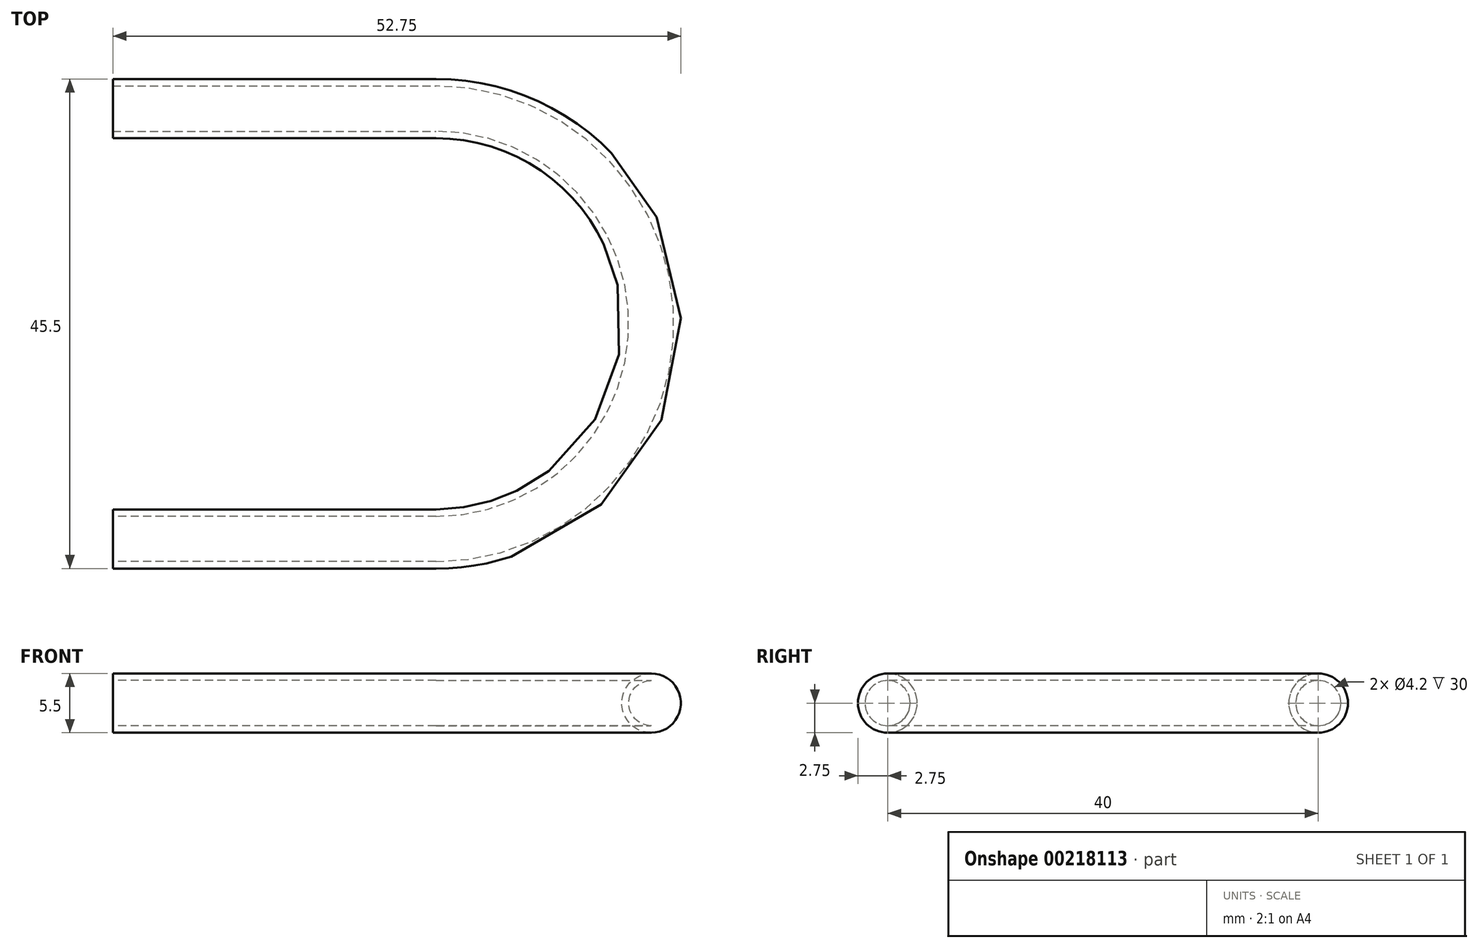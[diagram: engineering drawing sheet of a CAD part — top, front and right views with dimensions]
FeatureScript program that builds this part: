
annotation { "Feature Type Name" : "Feature", "Feature Type Description" : "" }
export const myFeature = defineFeature(function(context is Context, id is Id, definition is map)
    precondition{}
    {
        {
            var Q0;
            Q0=qCreatedBy(makeId("Top.planeOp"),FACE);
            var sketch = newSketch(context, id + "F0", { "sketchPlane" : qUnion([Q0])});
            skLineSegment(sketch, "E0.bottom", {"start": v(5, -20) * mm, "end": v(-25, -20) * mm});
            skLineSegment(sketch, "E0.top", {"start": v(5, 20) * mm, "end": v(-25, 20) * mm});
            skPoint(sketch, "E0.middle", {"position": v(0, 0) * mm});
            skLineSegment(sketch, "E1", {"start": v(5, 27.25) * mm, "end": v(5, -32.25) * mm, "construction": true});
            skArc(sketch, "E2", {"start": v(5, -20) * mm, "mid": v(25, 0) * mm, "end": v(5, 20) * mm});
            skPoint(sketch, "E3.orphan", {"position": v(25, 20) * mm});
            skPoint(sketch, "E4.orphan", {"position": v(25, -20) * mm});
            skSolve(sketch);
        }
        {
            var Q0;
            Q0=qCreatedBy(makeId("Right.planeOp"),FACE);
            cPlane(context, id + "F1", {"entities" : qUnion([Q0]), "cplaneType" : CPlaneType.OFFSET, "offset" : 25 * mm, "oppositeDirection" : true, "width" : 150 * mm, "height" : 150 * mm});
        }
        {
            var Q0;
            Q0=qCreatedBy(id+"F1.planeOp",FACE);
            var sketch = newSketch(context, id + "F2", { "sketchPlane" : qUnion([Q0])});
            skCircle(sketch, "E5", {"center": v(20, 0) * mm, "radius": 2.1 * mm});
            skCircle(sketch, "E6", {"center": v(20, 0) * mm, "radius": 2.75 * mm});
            skSolve(sketch);
        }
        {
            var Q0;
            Q0=makeQuery(id+"F2.imprint","IMPRINT",FACE,{"disambiguationData":[TD([[makeQuery(id+"F2.imprint","IMPRINT",EDGE,{"derivedFrom":sQuery(id+"F2.wireOp",EDGE,"E5")}),-1.0]])]});
            var Q1;
            Q1=sQuery(id+"F0.wireOp",EDGE,"E0.top");
            var Q2;
            Q2=sQuery(id+"F0.wireOp",EDGE,"E2");
            var Q3;
            Q3=sQuery(id+"F0.wireOp",EDGE,"E0.bottom");
            sweep(context, id + "F3", {"profiles" : qUnion([Q0]), "path" : qUnion([Q1, Q2, Q3])});
        }
    });
